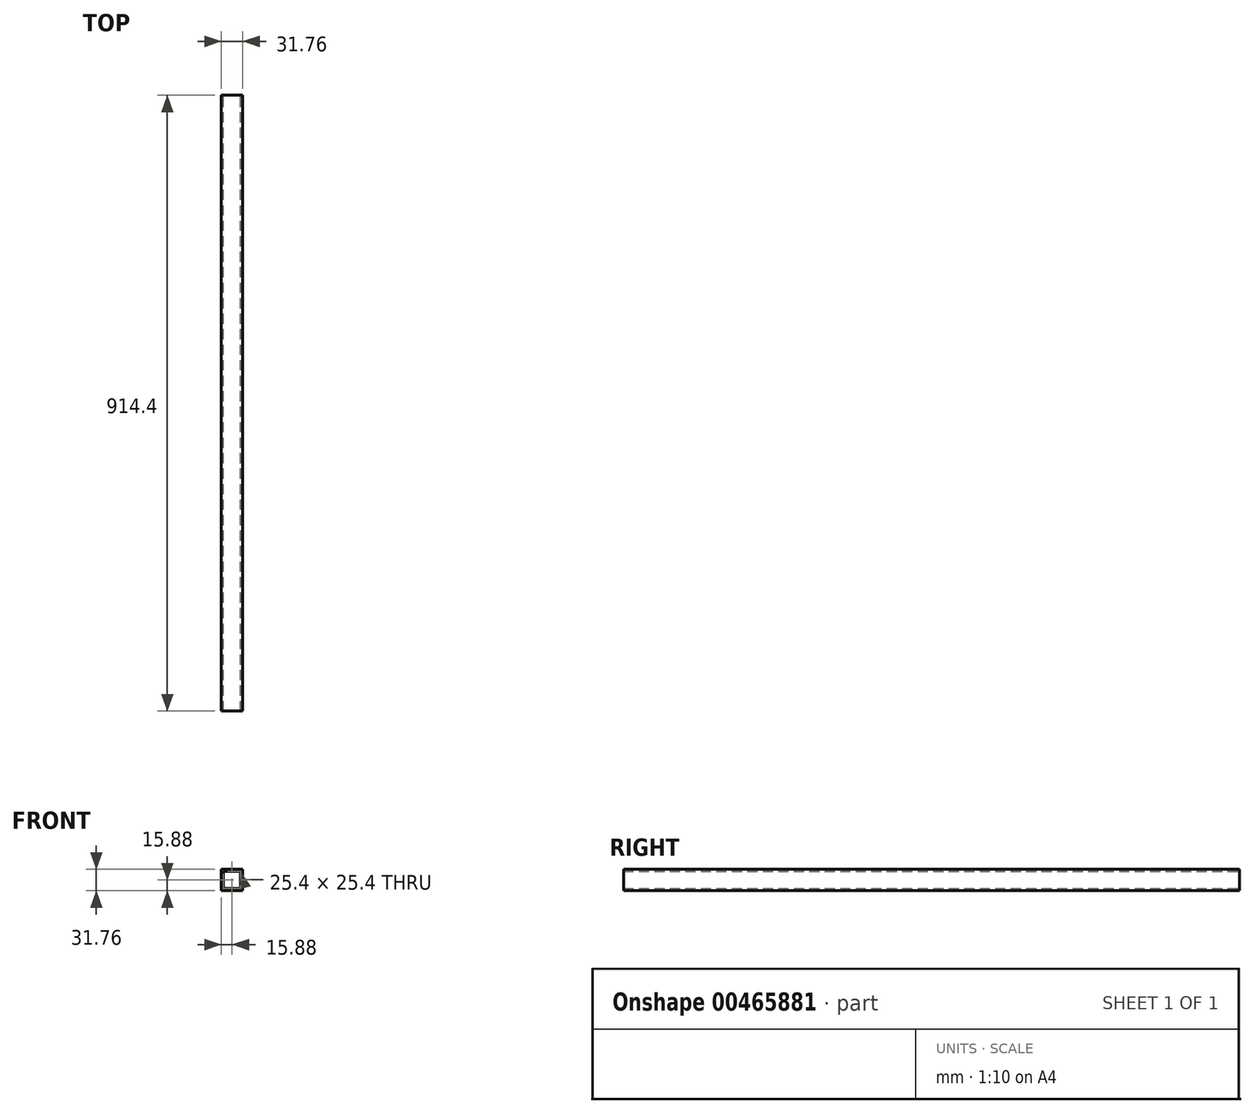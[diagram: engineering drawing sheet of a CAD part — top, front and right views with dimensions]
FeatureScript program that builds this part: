
annotation { "Feature Type Name" : "Feature", "Feature Type Description" : "" }
export const myFeature = defineFeature(function(context is Context, id is Id, definition is map)
    precondition{}
    {
        {
            var Q0;
            Q0=qCreatedBy(makeId("Front.planeOp"),FACE);
            var sketch = newSketch(context, id + "F0", { "sketchPlane" : qUnion([Q0])});
            skLineSegment(sketch, "E0.bottom", {"start": v(-15.87, 15.87) * mm, "end": v(15.88, 15.87) * mm});
            skLineSegment(sketch, "E0.top", {"start": v(-15.88, -15.88) * mm, "end": v(15.87, -15.88) * mm});
            skLineSegment(sketch, "E0.left", {"start": v(-15.87, 15.87) * mm, "end": v(-15.88, -15.88) * mm});
            skLineSegment(sketch, "E0.right", {"start": v(15.88, 15.87) * mm, "end": v(15.87, -15.88) * mm});
            skPoint(sketch, "E0.middle", {"position": v(0, 0) * mm});
            skLineSegment(sketch, "E1.bottom", {"start": v(-12.7, 12.7) * mm, "end": v(12.7, 12.7) * mm});
            skLineSegment(sketch, "E1.top", {"start": v(-12.7, -12.7) * mm, "end": v(12.7, -12.7) * mm});
            skLineSegment(sketch, "E1.left", {"start": v(-12.7, 12.7) * mm, "end": v(-12.7, -12.7) * mm});
            skLineSegment(sketch, "E1.right", {"start": v(12.7, 12.7) * mm, "end": v(12.7, -12.7) * mm});
            skSolve(sketch);
        }
        {
            var Q0;
            Q0=makeQuery(id+"F0.imprint","IMPRINT",FACE,{"disambiguationData":[TD([[makeQuery(id+"F0.imprint","IMPRINT",EDGE,{"derivedFrom":sQuery(id+"F0.wireOp",EDGE,"E0.bottom")}),-1.0]])]});
            extrude(context, id + "F1", {"entities" : qUnion([Q0]), "endBound" : BoundingType.SYMMETRIC, "depth" : 914.4 * mm});
        }
    });
